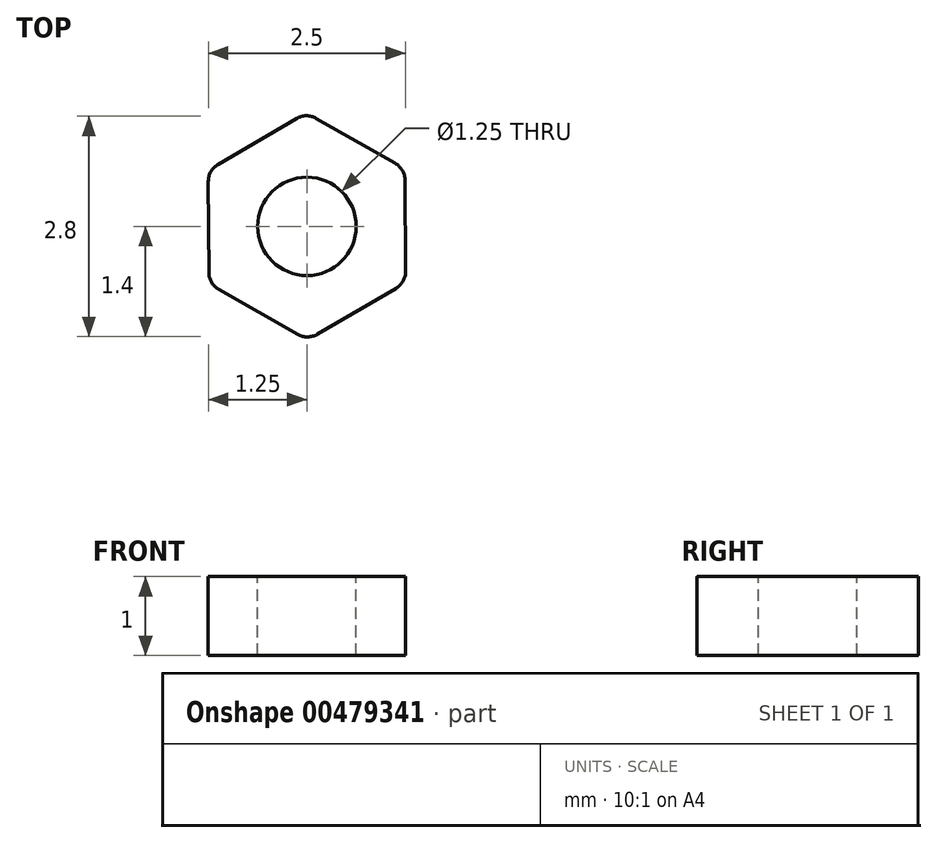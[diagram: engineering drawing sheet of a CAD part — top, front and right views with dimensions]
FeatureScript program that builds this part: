
annotation { "Feature Type Name" : "Feature", "Feature Type Description" : "" }
export const myFeature = defineFeature(function(context is Context, id is Id, definition is map)
    precondition{}
    {
        {
            var Q0;
            Q0=qCreatedBy(makeId("Top.planeOp"),FACE);
            var sketch = newSketch(context, id + "F0", { "sketchPlane" : qUnion([Q0])});
            skCircle(sketch, "E0.cCircle", {"center": v(0, 0) * mm, "radius": 5 * mm, "construction": true});
            skLineSegment(sketch, "E0.0", {"start": v(5.02, -2.85) * mm, "end": v(0.04, -5.77) * mm});
            skLineSegment(sketch, "E0.1", {"start": v(0.04, -5.77) * mm, "end": v(-4.98, -2.92) * mm});
            skLineSegment(sketch, "E0.2", {"start": v(-4.98, -2.92) * mm, "end": v(-5.02, 2.85) * mm});
            skLineSegment(sketch, "E0.3", {"start": v(-5.02, 2.85) * mm, "end": v(-0.04, 5.77) * mm});
            skLineSegment(sketch, "E0.4", {"start": v(-0.04, 5.77) * mm, "end": v(4.98, 2.92) * mm});
            skLineSegment(sketch, "E0.5", {"start": v(4.98, 2.92) * mm, "end": v(5.02, -2.85) * mm});
            skPoint(sketch, "E0.0.midPoint", {"position": v(2.53, -4.31) * mm});
            skSolve(sketch);
        }
        {
            var Q0;
            Q0=qSketchRegion(id+"F0",true);
            extrude(context, id + "F1", {"entities" : qUnion([Q0]), "depth" : 4 * mm});
        }
        {
            var Q0;
            Q0=makeQuery(id+"F1.opExtrude","CAP_FACE",FACE,{"disambiguationData":[OSD([sQuery(id+"F0.wireOp",EDGE,"E0.0"),sQuery(id+"F0.wireOp",EDGE,"E0.1"),sQuery(id+"F0.wireOp",EDGE,"E0.2"),sQuery(id+"F0.wireOp",EDGE,"E0.3"),sQuery(id+"F0.wireOp",EDGE,"E0.4"),sQuery(id+"F0.wireOp",EDGE,"E0.5")])],"isStart":false});
            var sketch = newSketch(context, id + "F2", { "sketchPlane" : qUnion([Q0])});
            skCircle(sketch, "E1", {"center": v(0, 0) * mm, "radius": 2.5 * mm});
            skSolve(sketch);
        }
        {
            var Q0;
            Q0=sQuery(id+"F2.wireOp",VERTEX,"E1.center");
            var Q1;
            Q1=makeQuery(id+"F1.opExtrude","SWEPT_BODY",BODY,{"disambiguationData":[OSD([sQuery(id+"F0.wireOp",EDGE,"E0.0"),sQuery(id+"F0.wireOp",EDGE,"E0.1"),sQuery(id+"F0.wireOp",EDGE,"E0.2"),sQuery(id+"F0.wireOp",EDGE,"E0.3"),sQuery(id+"F0.wireOp",EDGE,"E0.4"),sQuery(id+"F0.wireOp",EDGE,"E0.5")])]});
            hole(context, id + "F3", {"style" : HoleStyle.SIMPLE, "endStyle" : HoleEndStyle.BLIND, "holeDiameter" : 5 * mm, "holeDepth" : 10 * mm, "isTappedThrough" : true, "tappedDepth" : 12 * mm, "tapClearance" : 3, "locations" : qUnion([Q0]), "scope" : qUnion([Q1])});
        }
        {
            var Q0;
            Q0=makeQuery(id+"F1.opExtrude","SWEPT_EDGE",EDGE,{"disambiguationData":[OSD([sQuery(id+"F0.wireOp",EDGE,"E0.2"),sQuery(id+"F0.wireOp",EDGE,"E0.3")])]});
            var Q1;
            Q1=makeQuery(id+"F1.opExtrude","SWEPT_EDGE",EDGE,{"disambiguationData":[OSD([sQuery(id+"F0.wireOp",EDGE,"E0.3"),sQuery(id+"F0.wireOp",EDGE,"E0.4")])]});
            var Q2;
            Q2=makeQuery(id+"F1.opExtrude","SWEPT_EDGE",EDGE,{"disambiguationData":[OSD([sQuery(id+"F0.wireOp",EDGE,"E0.1"),sQuery(id+"F0.wireOp",EDGE,"E0.2")])]});
            var Q3;
            Q3=makeQuery(id+"F1.opExtrude","SWEPT_EDGE",EDGE,{"disambiguationData":[OSD([sQuery(id+"F0.wireOp",EDGE,"E0.0"),sQuery(id+"F0.wireOp",EDGE,"E0.1")])]});
            var Q4;
            Q4=makeQuery(id+"F1.opExtrude","SWEPT_EDGE",EDGE,{"disambiguationData":[OSD([sQuery(id+"F0.wireOp",EDGE,"E0.0"),sQuery(id+"F0.wireOp",EDGE,"E0.5")])]});
            var Q5;
            Q5=makeQuery(id+"F1.opExtrude","SWEPT_EDGE",EDGE,{"disambiguationData":[OSD([sQuery(id+"F0.wireOp",EDGE,"E0.4"),sQuery(id+"F0.wireOp",EDGE,"E0.5")])]});
            fillet(context, id + "F4", {"entities" : qUnion([Q0, Q1, Q2, Q3, Q4, Q5]), "radius" : 1 * mm, "tangentPropagation" : true, "allowEdgeOverflow" : false});
        }
        {
            var Q0;
            Q0=makeQuery(id+"F1.opExtrude","SWEPT_BODY",BODY,{"disambiguationData":[OSD([sQuery(id+"F0.wireOp",EDGE,"E0.0"),sQuery(id+"F0.wireOp",EDGE,"E0.1"),sQuery(id+"F0.wireOp",EDGE,"E0.2"),sQuery(id+"F0.wireOp",EDGE,"E0.3"),sQuery(id+"F0.wireOp",EDGE,"E0.4"),sQuery(id+"F0.wireOp",EDGE,"E0.5")])]});
            var Q1;
            Q1=qCreatedBy(makeId("Origin.pointOp"),VERTEX);
            transform(context, id + "F5", {"entities" : qUnion([Q0]), "transformType" : TransformType.SCALE_UNIFORMLY, "scale" : 0.25, "scalePoint" : qUnion([Q1]), "makeCopy" : false});
        }
    });
